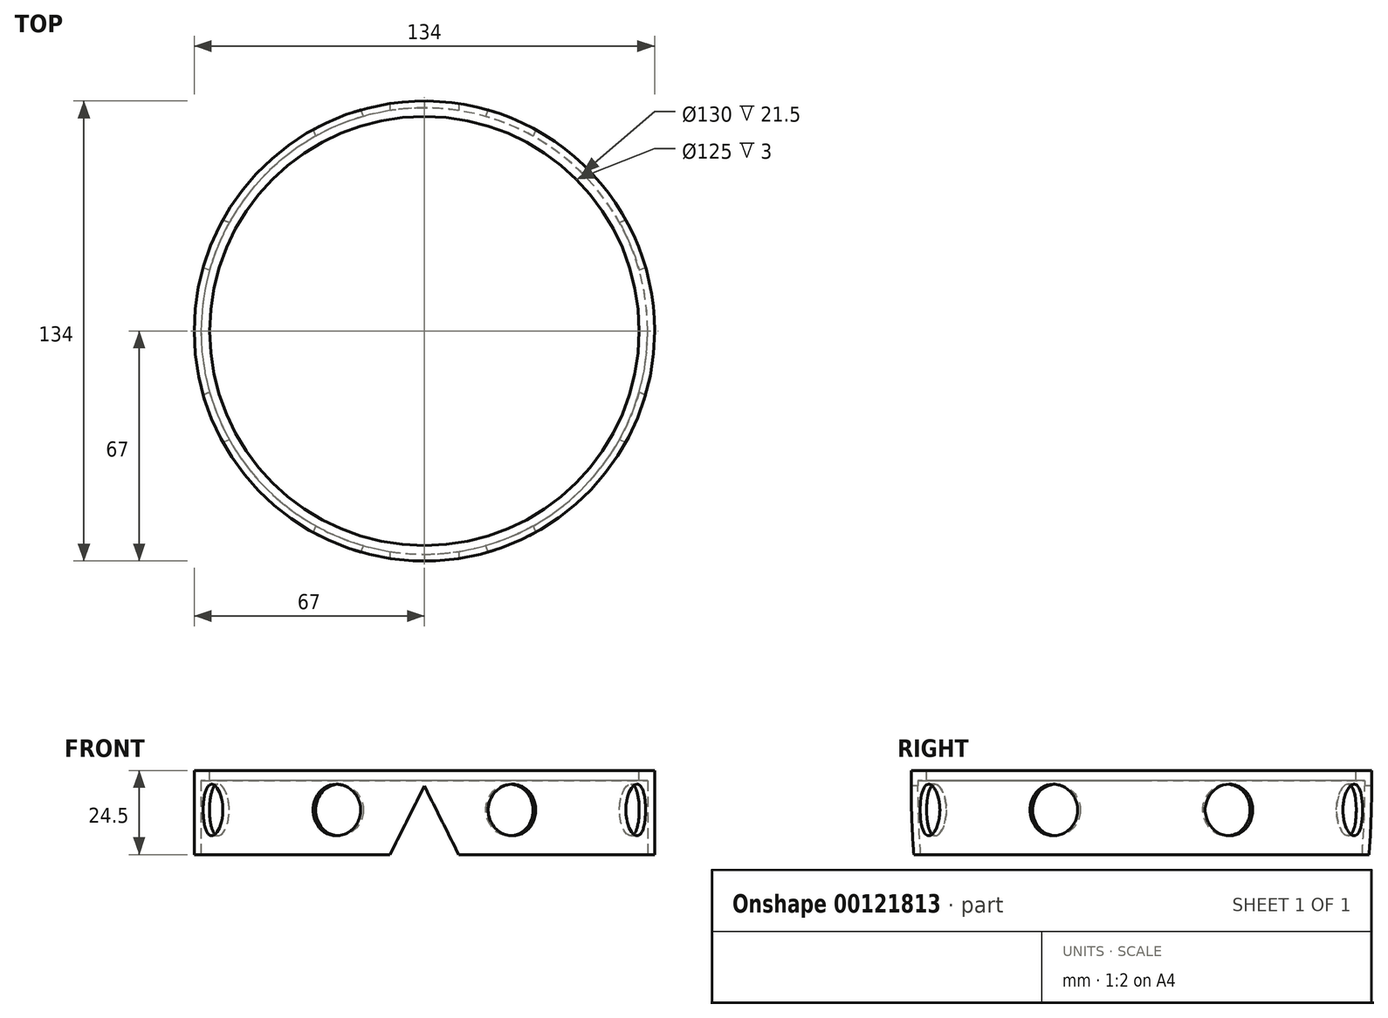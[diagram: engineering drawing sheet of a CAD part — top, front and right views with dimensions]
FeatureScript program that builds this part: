
annotation { "Feature Type Name" : "Feature", "Feature Type Description" : "" }
export const myFeature = defineFeature(function(context is Context, id is Id, definition is map)
    precondition{}
    {
        {
            var Q0;
            Q0=qCreatedBy(makeId("Top.planeOp"),FACE);
            var sketch = newSketch(context, id + "F0", { "sketchPlane" : qUnion([Q0])});
            skCircle(sketch, "E0", {"center": v(0, 0) * mm, "radius": 67 * mm});
            skCircle(sketch, "E1", {"center": v(0, 0) * mm, "radius": 65 * mm});
            skSolve(sketch);
        }
        {
            var Q0;
            Q0 = qSketchRegion(id + "F0", true);
            extrude(context, id + "F1", {"entities" : qUnion([Q0]), "depth" : 24.5 * mm});
        }
        {
            var Q0;
            Q0=qCreatedBy(makeId("Front.planeOp"),FACE);
            var sketch = newSketch(context, id + "F2", { "sketchPlane" : qUnion([Q0])});
            skCircle(sketch, "E2.cCircle", {"center": v(0, -39.45) * mm, "radius": 7.18 * mm, "construction": true});
            skLineSegment(sketch, "E2.0", {"start": v(0, -32.27) * mm, "end": v(6.21, -43.04) * mm});
            skLineSegment(sketch, "E2.1", {"start": v(6.21, -43.04) * mm, "end": v(-6.21, -43.04) * mm});
            skLineSegment(sketch, "E2.2", {"start": v(-6.21, -43.04) * mm, "end": v(0, -32.27) * mm});
            skLineSegment(sketch, "E3", {"start": v(0, 20) * mm, "end": v(-10, 0) * mm});
            skLineSegment(sketch, "E4", {"start": v(-10, 0) * mm, "end": v(10, 0) * mm});
            skLineSegment(sketch, "E5", {"start": v(10, 0) * mm, "end": v(0, 20) * mm});
            skSolve(sketch);
        }
        {
            var Q0;
            Q0 = qSketchRegion(id + "F2", true);
            extrude(context, id + "F3", {"entities" : qUnion([Q0]), "operationType" : NewBodyOperationType.REMOVE, "endBound" : BoundingType.SYMMETRIC, "oppositeDirection" : true, "depth" : 250 * mm});
        }
        {
            var Q0;
            Q0=qCreatedBy(makeId("Right.planeOp"),FACE);
            var sketch = newSketch(context, id + "F4", { "sketchPlane" : qUnion([Q0])});
            skLineSegment(sketch, "E6", {"start": v(0, 0) * mm, "end": v(10, 0) * mm});
            skLineSegment(sketch, "E7", {"start": v(10, 0) * mm, "end": v(0, 20) * mm});
            skLineSegment(sketch, "E8", {"start": v(0, 0) * mm, "end": v(-10, 0) * mm});
            skLineSegment(sketch, "E9", {"start": v(-10, 0) * mm, "end": v(0, 20) * mm});
            skSolve(sketch);
        }
        {
            var Q0;
            Q0=makeQuery(id+"F1.opExtrude","CAP_FACE",FACE,{"disambiguationData":[OSD([sQuery(id+"F0.wireOp",EDGE,"E0"),sQuery(id+"F0.wireOp",EDGE,"E1")])],"isStart":false});
            var sketch = newSketch(context, id + "F5", { "sketchPlane" : qUnion([Q0])});
            skLineSegment(sketch, "E10", {"start": v(0, 0) * mm, "end": v(27.66, -66.79) * mm});
            skLineSegment(sketch, "E11", {"start": v(0, 0) * mm, "end": v(71.72, -29.7) * mm});
            skLineSegment(sketch, "E12", {"start": v(0, 0) * mm, "end": v(67.07, 27.78) * mm});
            skLineSegment(sketch, "E13", {"start": v(0, 0) * mm, "end": v(28.95, 69.9) * mm});
            skLineSegment(sketch, "E14", {"start": v(0, 0) * mm, "end": v(-25.64, 61.9) * mm});
            skLineSegment(sketch, "E15", {"start": v(0, 0) * mm, "end": v(-61.9, 25.64) * mm});
            skLineSegment(sketch, "E16", {"start": v(0, 0) * mm, "end": v(-61.9, -25.64) * mm});
            skLineSegment(sketch, "E17", {"start": v(0, 0) * mm, "end": v(-25.64, -61.9) * mm});
            skSolve(sketch);
        }
        {
            var Q0;
            Q0=sQuery(id+"F5.wireOp",VERTEX,"E17.end");
            var Q1;
            {var subQ0=sQuery(id+"F0.wireOp",EDGE,"E0");Q1=makeQuery(id+"F3.boolean.opBoolean","SPLIT",EDGE,{"disambiguationData":[TD([makeQuery(id+"F3.opExtrude","SWEPT_FACE",FACE,{"disambiguationData":[OSD([sQuery(id+"F2.wireOp",EDGE,"E3")])]})])],"derivedFrom":makeQuery(id+"F1.opExtrude","CAP_EDGE",EDGE,{"disambiguationData":[OSD([subQ0])],"isStart":true})});}
            cPlane(context, id + "F6", {"entities" : qUnion([Q0, Q1]), "cplaneType" : CPlaneType.CURVE_POINT, "offset" : 25 * mm, "width" : 150 * mm, "height" : 150 * mm});
        }
        {
            var Q0;
            Q0=qCreatedBy(id+"F6.planeOp",FACE);
            var sketch = newSketch(context, id + "F7", { "sketchPlane" : qUnion([Q0])});
            skLineSegment(sketch, "E18", {"start": v(0, 0) * mm, "end": v(0, 13) * mm});
            skCircle(sketch, "E19", {"center": v(0, 13) * mm, "radius": 7.5 * mm});
            skSolve(sketch);
        }
        {
            var Q0;
            Q0 = qSketchRegion(id + "F7", true);
            extrude(context, id + "F8", {"entities" : qUnion([Q0]), "operationType" : NewBodyOperationType.REMOVE, "endBound" : BoundingType.SYMMETRIC, "oppositeDirection" : true, "depth" : 250 * mm});
        }
        {
            var Q0;
            Q0=sQuery(id+"F5.wireOp",VERTEX,"E14.end");
            var Q1;
            {var subQ0=sQuery(id+"F0.wireOp",EDGE,"E0");Q1=makeQuery(id+"F3.boolean.opBoolean","SPLIT",EDGE,{"disambiguationData":[TD([makeQuery(id+"F3.opExtrude","SWEPT_FACE",FACE,{"disambiguationData":[OSD([sQuery(id+"F2.wireOp",EDGE,"E3")])]})])],"derivedFrom":makeQuery(id+"F1.opExtrude","CAP_EDGE",EDGE,{"disambiguationData":[OSD([subQ0])],"isStart":true})});}
            cPlane(context, id + "F9", {"entities" : qUnion([Q0, Q1]), "cplaneType" : CPlaneType.CURVE_POINT, "offset" : 25 * mm, "width" : 150 * mm, "height" : 150 * mm});
        }
        {
            var Q0;
            Q0=sQuery(id+"F5.wireOp",VERTEX,"E15.end");
            var Q1;
            {var subQ0=sQuery(id+"F0.wireOp",EDGE,"E0");Q1=makeQuery(id+"F3.boolean.opBoolean","SPLIT",EDGE,{"disambiguationData":[TD([makeQuery(id+"F3.opExtrude","SWEPT_FACE",FACE,{"disambiguationData":[OSD([sQuery(id+"F2.wireOp",EDGE,"E3")])]})])],"derivedFrom":makeQuery(id+"F1.opExtrude","CAP_EDGE",EDGE,{"disambiguationData":[OSD([subQ0])],"isStart":true})});}
            cPlane(context, id + "F10", {"entities" : qUnion([Q0, Q1]), "cplaneType" : CPlaneType.CURVE_POINT, "offset" : 25 * mm, "width" : 150 * mm, "height" : 150 * mm});
        }
        {
            var Q0;
            Q0=qCreatedBy(id+"F9.planeOp",FACE);
            var sketch = newSketch(context, id + "F11", { "sketchPlane" : qUnion([Q0])});
            skCircle(sketch, "E20", {"center": v(0, 13) * mm, "radius": 7.5 * mm});
            skSolve(sketch);
        }
        {
            var Q0;
            Q0 = qSketchRegion(id + "F11", true);
            extrude(context, id + "F12", {"entities" : qUnion([Q0]), "operationType" : NewBodyOperationType.REMOVE, "endBound" : BoundingType.SYMMETRIC, "depth" : 250 * mm});
        }
        {
            var Q0;
            Q0=qCreatedBy(id+"F10.planeOp",FACE);
            var sketch = newSketch(context, id + "F13", { "sketchPlane" : qUnion([Q0])});
            skLineSegment(sketch, "E21", {"start": v(0, 0) * mm, "end": v(0, 13) * mm});
            skCircle(sketch, "E22", {"center": v(0, 13) * mm, "radius": 7.5 * mm});
            skSolve(sketch);
        }
        {
            var Q0;
            Q0 = qSketchRegion(id + "F13", true);
            extrude(context, id + "F14", {"entities" : qUnion([Q0]), "operationType" : NewBodyOperationType.REMOVE, "endBound" : BoundingType.SYMMETRIC, "oppositeDirection" : true, "depth" : 250 * mm});
        }
        {
            var Q0;
            Q0=sQuery(id+"F5.wireOp",VERTEX,"E16.end");
            var Q1;
            {var subQ0=sQuery(id+"F0.wireOp",EDGE,"E0");Q1=makeQuery(id+"F3.boolean.opBoolean","SPLIT",EDGE,{"disambiguationData":[TD([makeQuery(id+"F3.opExtrude","SWEPT_FACE",FACE,{"disambiguationData":[OSD([sQuery(id+"F2.wireOp",EDGE,"E3")])]})])],"derivedFrom":makeQuery(id+"F1.opExtrude","CAP_EDGE",EDGE,{"disambiguationData":[OSD([subQ0])],"isStart":true})});}
            cPlane(context, id + "F15", {"entities" : qUnion([Q0, Q1]), "cplaneType" : CPlaneType.CURVE_POINT, "offset" : 25 * mm, "width" : 150 * mm, "height" : 150 * mm});
        }
        {
            var Q0;
            Q0=qCreatedBy(id+"F15.planeOp",FACE);
            var sketch = newSketch(context, id + "F16", { "sketchPlane" : qUnion([Q0])});
            skLineSegment(sketch, "E23", {"start": v(0, 0) * mm, "end": v(0, 13) * mm});
            skCircle(sketch, "E24", {"center": v(0, 13) * mm, "radius": 7.5 * mm});
            skSolve(sketch);
        }
        {
            var Q0;
            Q0 = qSketchRegion(id + "F16", true);
            extrude(context, id + "F17", {"entities" : qUnion([Q0]), "operationType" : NewBodyOperationType.REMOVE, "endBound" : BoundingType.SYMMETRIC, "oppositeDirection" : true, "depth" : 250 * mm});
        }
        {
            var Q0;
            Q0=makeQuery(id+"F1.opExtrude","CAP_FACE",FACE,{"disambiguationData":[OSD([sQuery(id+"F0.wireOp",EDGE,"E0"),sQuery(id+"F0.wireOp",EDGE,"E1")])],"isStart":false});
            var sketch = newSketch(context, id + "F18", { "sketchPlane" : qUnion([Q0])});
            skCircle(sketch, "E25", {"center": v(0, 0) * mm, "radius": 62.5 * mm});
            skCircle(sketch, "E26", {"center": v(0, 0) * mm, "radius": 67 * mm});
            skSolve(sketch);
        }
        {
            var Q0;
            Q0 = qSketchRegion(id + "F18", true);
            extrude(context, id + "F19", {"entities" : qUnion([Q0]), "operationType" : NewBodyOperationType.ADD, "oppositeDirection" : true, "depth" : 3 * mm});
        }
    });
